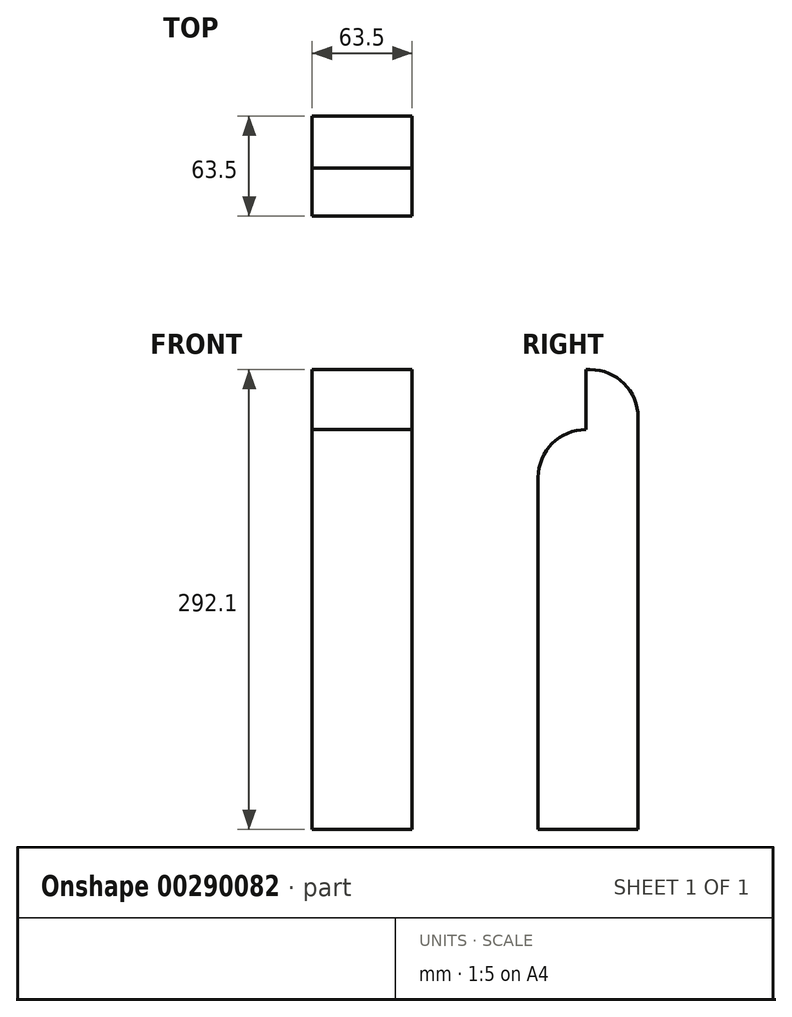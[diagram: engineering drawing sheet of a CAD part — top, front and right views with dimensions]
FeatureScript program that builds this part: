
annotation { "Feature Type Name" : "Feature", "Feature Type Description" : "" }
export const myFeature = defineFeature(function(context is Context, id is Id, definition is map)
    precondition{}
    {
        {
            var Q0;
            Q0=qCreatedBy(makeId("Top.planeOp"),FACE);
            var sketch = newSketch(context, id + "F0", { "sketchPlane" : qUnion([Q0])});
            skLineSegment(sketch, "E0.bottom", {"start": v(0, 0) * mm, "end": v(63.5, 0) * mm});
            skLineSegment(sketch, "E0.top", {"start": v(0, 63.5) * mm, "end": v(63.5, 63.5) * mm});
            skLineSegment(sketch, "E0.left", {"start": v(0, 0) * mm, "end": v(0, 63.5) * mm});
            skLineSegment(sketch, "E0.right", {"start": v(63.5, 0) * mm, "end": v(63.5, 63.5) * mm});
            skSolve(sketch);
        }
        {
            var Q0;
            Q0 = qSketchRegion(id + "F0", true);
            extrude(context, id + "F1", {"entities" : qUnion([Q0]), "depth" : 254 * mm});
        }
        {
            var Q0;
            Q0=makeQuery(id+"F1.opExtrude","CAP_EDGE",EDGE,{"disambiguationData":[OSD([sQuery(id+"F0.wireOp",EDGE,"E0.bottom")])],"isStart":false});
            fillet(context, id + "F2", {"entities" : qUnion([Q0]), "radius" : 30.48 * mm, "tangentPropagation" : true, "allowEdgeOverflow" : false});
        }
        {
            var Q0;
            Q0=makeQuery(id+"F1.opExtrude","CAP_FACE",FACE,{"disambiguationData":[OSD([sQuery(id+"F0.wireOp",EDGE,"E0.bottom"),sQuery(id+"F0.wireOp",EDGE,"E0.top"),sQuery(id+"F0.wireOp",EDGE,"E0.left"),sQuery(id+"F0.wireOp",EDGE,"E0.right")])],"isStart":false});
            var sketch = newSketch(context, id + "F3", { "sketchPlane" : qUnion([Q0])});
            skSolve(sketch);
        }
        {
            var Q0;
            {var subQ0=sQuery(id+"F0.wireOp",EDGE,"E0.top");Q0=makeQuery(id+"F3.imprint","IMPRINT",FACE,{"disambiguationData":[TD([[makeQuery(id+"F3.imprint","IMPRINT",EDGE,{"derivedFrom":makeQuery(id+"F1.opExtrude","CAP_EDGE",EDGE,{"disambiguationData":[OSD([subQ0])],"isStart":false})}),-1.0]])]});}
            extrude(context, id + "F4", {"entities" : qUnion([Q0]), "operationType" : NewBodyOperationType.ADD, "depth" : 38.1 * mm});
        }
        {
            var Q0;
            Q0=makeQuery(id+"F4.opExtrude","CAP_EDGE",EDGE,{"disambiguationData":[OSD([sQuery(id+"F0.wireOp",EDGE,"E0.top")])],"isStart":false});
            fillet(context, id + "F5", {"entities" : qUnion([Q0]), "radius" : 30.48 * mm, "tangentPropagation" : true, "allowEdgeOverflow" : false});
        }
    });
